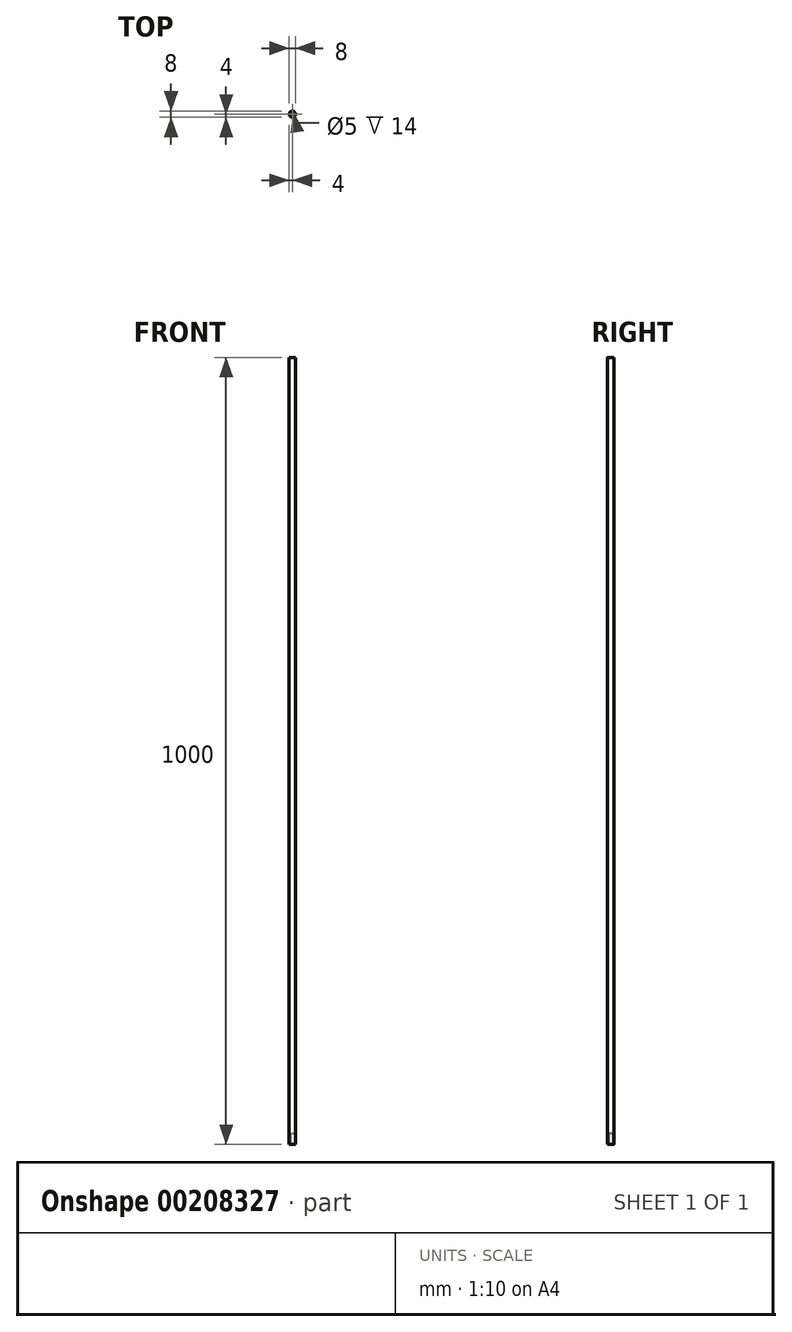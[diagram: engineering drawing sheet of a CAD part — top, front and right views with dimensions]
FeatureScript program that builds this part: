
annotation { "Feature Type Name" : "Feature", "Feature Type Description" : "" }
export const myFeature = defineFeature(function(context is Context, id is Id, definition is map)
    precondition{}
    {
        {
            var Q0;
            Q0=qCreatedBy(makeId("Top.planeOp"),FACE);
            var sketch = newSketch(context, id + "F0", { "sketchPlane" : qUnion([Q0])});
            skCircle(sketch, "E0", {"center": v(0, 0) * mm, "radius": 4 * mm});
            skSolve(sketch);
        }
        {
            var Q0;
            Q0=qSketchRegion(id+"F0",true);
            extrude(context, id + "F1", {"entities" : qUnion([Q0]), "depth" : 1000 * mm});
        }
        {
            var Q0;
            Q0=makeQuery(id+"F1.opExtrude","CAP_FACE",FACE,{"disambiguationData":[OSD([sQuery(id+"F0.wireOp",EDGE,"E0")])],"isStart":true});
            var sketch = newSketch(context, id + "F2", { "sketchPlane" : qUnion([Q0])});
            skCircle(sketch, "E1", {"center": v(0, 0) * mm, "radius": 2.5 * mm});
            skSolve(sketch);
        }
        {
            var Q0;
            Q0=qSketchRegion(id+"F2",true);
            extrude(context, id + "F3", {"entities" : qUnion([Q0]), "operationType" : NewBodyOperationType.REMOVE, "oppositeDirection" : true, "depth" : 14 * mm});
        }
    });
